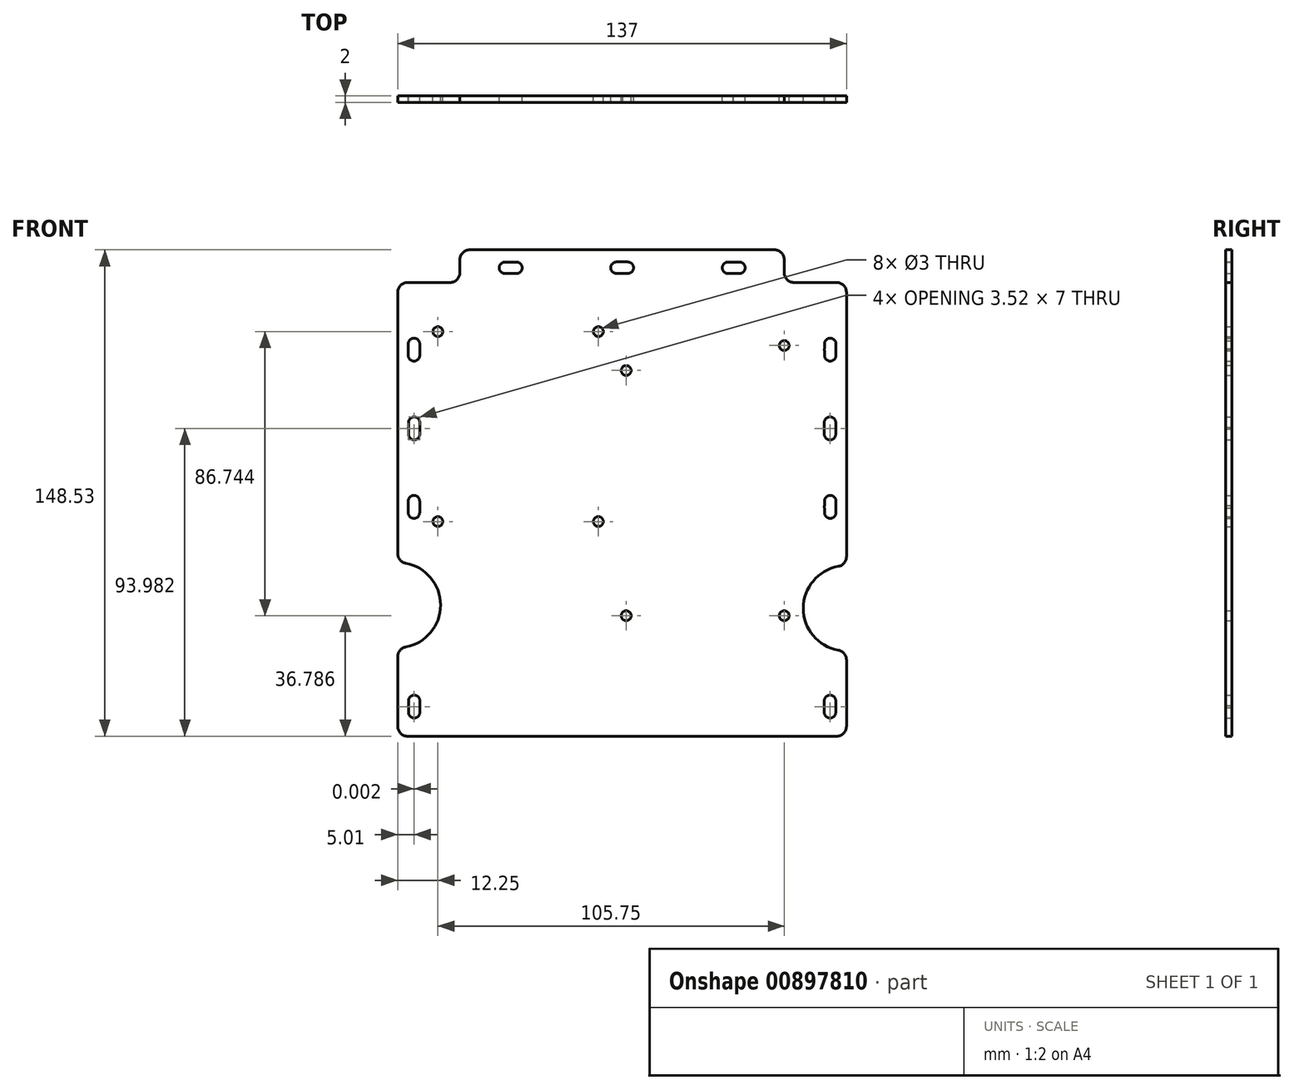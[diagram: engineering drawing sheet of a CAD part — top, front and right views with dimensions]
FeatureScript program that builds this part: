
annotation { "Feature Type Name" : "Feature", "Feature Type Description" : "" }
export const myFeature = defineFeature(function(context is Context, id is Id, definition is map)
    precondition{}
    {
        {
            var Q0;
            Q0=qCreatedBy(makeId("Front.planeOp"),FACE);
            var sketch = newSketch(context, id + "F0", { "sketchPlane" : qUnion([Q0])});
            skLineSegment(sketch, "E0", {"start": v(-49.5, 105.5) * mm, "end": v(-49.5, 101.5) * mm});
            skLineSegment(sketch, "E1", {"start": v(-52.5, 98.5) * mm, "end": v(-65.5, 98.5) * mm});
            skLineSegment(sketch, "E2", {"start": v(-68.5, 95.5) * mm, "end": v(-68.5, 15.73) * mm});
            skLineSegment(sketch, "E3", {"start": v(-46.5, 108.5) * mm, "end": v(0, 108.5) * mm});
            skLineSegment(sketch, "E4.MirrorCS", {"start": v(46.5, 108.5) * mm, "end": v(0, 108.5) * mm});
            skLineSegment(sketch, "E5.MirrorCS", {"start": v(49.5, 105.5) * mm, "end": v(49.5, 101.5) * mm});
            skLineSegment(sketch, "E6.MirrorCS", {"start": v(68.5, 95.5) * mm, "end": v(68.5, 14.76) * mm});
            skPoint(sketch, "E7.visualSharp", {"position": v(-68.5, 98.5) * mm});
            skArc(sketch, "E7.filletArc", {"start": v(-65.5, 98.5) * mm, "mid": v(-67.62, 97.62) * mm, "end": v(-68.5, 95.5) * mm});
            skPoint(sketch, "E8.visualSharp", {"position": v(-49.5, 98.5) * mm});
            skArc(sketch, "E8.filletArc", {"start": v(-52.5, 98.5) * mm, "mid": v(-50.38, 99.38) * mm, "end": v(-49.5, 101.5) * mm});
            skPoint(sketch, "E9.visualSharp", {"position": v(-49.5, 108.5) * mm});
            skArc(sketch, "E9.filletArc", {"start": v(-46.5, 108.5) * mm, "mid": v(-48.62, 107.62) * mm, "end": v(-49.5, 105.5) * mm});
            skPoint(sketch, "E10.visualSharp", {"position": v(49.5, 108.5) * mm});
            skArc(sketch, "E10.filletArc", {"start": v(49.5, 105.5) * mm, "mid": v(48.62, 107.62) * mm, "end": v(46.5, 108.5) * mm});
            skPoint(sketch, "E11.visualSharp", {"position": v(49.5, 98.5) * mm});
            skArc(sketch, "E11.filletArc", {"start": v(49.5, 101.5) * mm, "mid": v(50.38, 99.38) * mm, "end": v(52.5, 98.5) * mm});
            skPoint(sketch, "E12.visualSharp", {"position": v(68.5, 98.5) * mm});
            skArc(sketch, "E12.filletArc", {"start": v(68.5, 95.5) * mm, "mid": v(67.62, 97.62) * mm, "end": v(65.5, 98.5) * mm});
            skCircle(sketch, "E13", {"center": v(0, 103) * mm, "radius": 1.75 * mm});
            skCircle(sketch, "E14", {"center": v(-34, 103) * mm, "radius": 1.75 * mm});
            skCircle(sketch, "E15", {"center": v(34, 103) * mm, "radius": 1.75 * mm});
            skPoint(sketch, "E16.centerSnap0", {"position": v(-59, 98.5) * mm});
            skCircle(sketch, "E17", {"center": v(-63.5, 54) * mm, "radius": 1.75 * mm});
            skCircle(sketch, "E18", {"center": v(-63.5, 30) * mm, "radius": 1.75 * mm});
            skCircle(sketch, "E19", {"center": v(-63.5, 78) * mm, "radius": 1.75 * mm});
            skCircle(sketch, "E20.MirrorC", {"center": v(63.5, 78) * mm, "radius": 1.75 * mm});
            skCircle(sketch, "E21.MirrorC", {"center": v(63.5, 54) * mm, "radius": 1.75 * mm});
            skCircle(sketch, "E22.MirrorC", {"center": v(63.5, 30) * mm, "radius": 1.75 * mm});
            skCircle(sketch, "E23", {"center": v(-63.5, -31) * mm, "radius": 1.75 * mm});
            skCircle(sketch, "E24.MirrorC", {"center": v(63.5, -31) * mm, "radius": 1.75 * mm});
            skLineSegment(sketch, "E25", {"start": v(-35.75, 103) * mm, "end": v(-32.25, 103) * mm});
            skArc(sketch, "E26.0.startCap", {"start": v(-35.75, 101.25) * mm, "mid": v(-37.5, 103) * mm, "end": v(-35.75, 104.75) * mm});
            skArc(sketch, "E26.0.endCap", {"start": v(-32.25, 104.75) * mm, "mid": v(-30.5, 103) * mm, "end": v(-32.25, 101.25) * mm});
            skLineSegment(sketch, "E26.0.left", {"start": v(-35.75, 104.75) * mm, "end": v(-32.25, 104.75) * mm});
            skLineSegment(sketch, "E26.0.right", {"start": v(-35.75, 101.25) * mm, "end": v(-32.25, 101.25) * mm});
            skArc(sketch, "E27.0.startCap", {"start": v(-1.74, 101.27) * mm, "mid": v(-3.5, 103.02) * mm, "end": v(-1.74, 104.77) * mm});
            skArc(sketch, "E27.0.endCap", {"start": v(1.76, 104.77) * mm, "mid": v(3.5, 103.02) * mm, "end": v(1.76, 101.27) * mm});
            skLineSegment(sketch, "E27.0.left", {"start": v(-1.74, 104.77) * mm, "end": v(1.76, 104.77) * mm});
            skLineSegment(sketch, "E27.0.right", {"start": v(-1.74, 101.27) * mm, "end": v(1.76, 101.27) * mm});
            skArc(sketch, "E28.0.startCap", {"start": v(32.33, 101.25) * mm, "mid": v(30.58, 103) * mm, "end": v(32.33, 104.75) * mm});
            skArc(sketch, "E28.0.endCap", {"start": v(35.83, 104.75) * mm, "mid": v(37.58, 103) * mm, "end": v(35.83, 101.25) * mm});
            skLineSegment(sketch, "E28.0.left", {"start": v(32.33, 104.75) * mm, "end": v(35.83, 104.75) * mm});
            skLineSegment(sketch, "E28.0.right", {"start": v(32.33, 101.25) * mm, "end": v(35.83, 101.25) * mm});
            skLineSegment(sketch, "E29", {"start": v(-63.53, 79.75) * mm, "end": v(-63.53, 76.25) * mm});
            skArc(sketch, "E30.0.startCap", {"start": v(-65.28, 79.75) * mm, "mid": v(-63.53, 81.5) * mm, "end": v(-61.78, 79.75) * mm});
            skArc(sketch, "E30.0.endCap", {"start": v(-61.78, 76.25) * mm, "mid": v(-63.53, 74.5) * mm, "end": v(-65.28, 76.25) * mm});
            skLineSegment(sketch, "E30.0.left", {"start": v(-61.78, 79.75) * mm, "end": v(-61.78, 76.25) * mm});
            skLineSegment(sketch, "E30.0.right", {"start": v(-65.28, 79.75) * mm, "end": v(-65.28, 76.25) * mm});
            skArc(sketch, "E31.0.startCap", {"start": v(-65.23, 55.7) * mm, "mid": v(-63.48, 57.45) * mm, "end": v(-61.73, 55.7) * mm});
            skArc(sketch, "E31.0.endCap", {"start": v(-61.73, 52.2) * mm, "mid": v(-63.48, 50.45) * mm, "end": v(-65.23, 52.2) * mm});
            skLineSegment(sketch, "E31.0.left", {"start": v(-61.73, 55.7) * mm, "end": v(-61.73, 52.2) * mm});
            skLineSegment(sketch, "E31.0.right", {"start": v(-65.23, 55.7) * mm, "end": v(-65.23, 52.2) * mm});
            skArc(sketch, "E32.0.startCap", {"start": v(-65.3, 31.74) * mm, "mid": v(-63.54, 33.5) * mm, "end": v(-61.8, 31.74) * mm});
            skArc(sketch, "E32.0.endCap", {"start": v(-61.8, 28.24) * mm, "mid": v(-63.54, 26.5) * mm, "end": v(-65.3, 28.24) * mm});
            skLineSegment(sketch, "E32.0.left", {"start": v(-61.8, 31.74) * mm, "end": v(-61.8, 28.24) * mm});
            skLineSegment(sketch, "E32.0.right", {"start": v(-65.3, 31.74) * mm, "end": v(-65.3, 28.24) * mm});
            skArc(sketch, "E33.MirrorCS", {"start": v(65.28, 79.75) * mm, "mid": v(63.53, 81.5) * mm, "end": v(61.78, 79.75) * mm});
            skLineSegment(sketch, "E34.MirrorCS", {"start": v(61.78, 79.75) * mm, "end": v(61.78, 76.25) * mm});
            skArc(sketch, "E35.MirrorCS", {"start": v(61.78, 76.25) * mm, "mid": v(63.53, 74.5) * mm, "end": v(65.28, 76.25) * mm});
            skLineSegment(sketch, "E36.MirrorCS", {"start": v(65.28, 79.75) * mm, "end": v(65.28, 76.25) * mm});
            skArc(sketch, "E37.MirrorCS", {"start": v(65.23, 55.7) * mm, "mid": v(63.48, 57.45) * mm, "end": v(61.73, 55.7) * mm});
            skLineSegment(sketch, "E38.MirrorCS", {"start": v(61.73, 55.7) * mm, "end": v(61.73, 52.2) * mm});
            skLineSegment(sketch, "E39.MirrorCS", {"start": v(65.23, 55.7) * mm, "end": v(65.23, 52.2) * mm});
            skArc(sketch, "E40.MirrorCS", {"start": v(61.73, 52.2) * mm, "mid": v(63.48, 50.45) * mm, "end": v(65.23, 52.2) * mm});
            skArc(sketch, "E41.MirrorCS", {"start": v(65.3, 31.74) * mm, "mid": v(63.54, 33.5) * mm, "end": v(61.8, 31.74) * mm});
            skLineSegment(sketch, "E42.MirrorCS", {"start": v(61.8, 31.74) * mm, "end": v(61.8, 28.24) * mm});
            skArc(sketch, "E43.MirrorCS", {"start": v(61.8, 28.24) * mm, "mid": v(63.54, 26.5) * mm, "end": v(65.3, 28.24) * mm});
            skLineSegment(sketch, "E44.MirrorCS", {"start": v(65.3, 31.74) * mm, "end": v(65.3, 28.24) * mm});
            skArc(sketch, "E45.0.startCap", {"start": v(-65.23, -29.25) * mm, "mid": v(-63.48, -27.5) * mm, "end": v(-61.73, -29.25) * mm});
            skArc(sketch, "E45.0.endCap", {"start": v(-61.73, -32.75) * mm, "mid": v(-63.48, -34.5) * mm, "end": v(-65.23, -32.75) * mm});
            skLineSegment(sketch, "E45.0.left", {"start": v(-61.73, -29.25) * mm, "end": v(-61.73, -32.75) * mm});
            skLineSegment(sketch, "E45.0.right", {"start": v(-65.23, -29.25) * mm, "end": v(-65.23, -32.75) * mm});
            skArc(sketch, "E46.MirrorCS", {"start": v(65.23, -29.25) * mm, "mid": v(63.48, -27.5) * mm, "end": v(61.73, -29.25) * mm});
            skLineSegment(sketch, "E47.MirrorCS", {"start": v(61.73, -29.25) * mm, "end": v(61.73, -32.75) * mm});
            skArc(sketch, "E48.MirrorCS", {"start": v(61.73, -32.75) * mm, "mid": v(63.48, -34.5) * mm, "end": v(65.23, -32.75) * mm});
            skLineSegment(sketch, "E49.MirrorCS", {"start": v(65.23, -29.25) * mm, "end": v(65.23, -32.75) * mm});
            skCircle(sketch, "E50", {"center": v(-56.25, 83.5) * mm, "radius": 1.5 * mm});
            skCircle(sketch, "E51", {"center": v(-56.25, 25.5) * mm, "radius": 1.5 * mm});
            skCircle(sketch, "E52", {"center": v(-7.25, 25.5) * mm, "radius": 1.5 * mm});
            skCircle(sketch, "E53", {"center": v(-7.25, 83.5) * mm, "radius": 1.5 * mm});
            skPoint(sketch, "E54.startSnap0", {"position": v(-68.42, 0) * mm});
            skArc(sketch, "E55", {"start": v(-66.05, 12.78) * mm, "mid": v(-55.42, 0) * mm, "end": v(-66.05, -12.78) * mm});
            skPoint(sketch, "E56.visualSharp", {"position": v(-68.5, 13) * mm});
            skArc(sketch, "E56.filletArc", {"start": v(-68.5, 15.73) * mm, "mid": v(-67.8, 13.81) * mm, "end": v(-66.05, 12.78) * mm});
            skPoint(sketch, "E57.visualSharp", {"position": v(-68.5, -13) * mm});
            skArc(sketch, "E57.filletArc", {"start": v(-66.05, -12.78) * mm, "mid": v(-67.8, -13.81) * mm, "end": v(-68.5, -15.73) * mm});
            skArc(sketch, "E58", {"start": v(66.03, 11.81) * mm, "mid": v(55.32, -0.98) * mm, "end": v(66.03, -13.78) * mm});
            skPoint(sketch, "E59.visualSharp", {"position": v(68.5, 12.01) * mm});
            skArc(sketch, "E59.filletArc", {"start": v(66.03, 11.81) * mm, "mid": v(67.8, 12.84) * mm, "end": v(68.5, 14.76) * mm});
            skPoint(sketch, "E60.visualSharp", {"position": v(68.5, -13.98) * mm});
            skArc(sketch, "E60.filletArc", {"start": v(68.5, -16.73) * mm, "mid": v(67.8, -14.8) * mm, "end": v(66.03, -13.78) * mm});
            skCircle(sketch, "E61", {"center": v(1.25, 71.66) * mm, "radius": 1.5 * mm});
            skCircle(sketch, "E62", {"center": v(1.25, -3.24) * mm, "radius": 1.5 * mm});
            skCircle(sketch, "E63", {"center": v(49.5, 79.26) * mm, "radius": 1.5 * mm});
            skCircle(sketch, "E64", {"center": v(49.5, -3.24) * mm, "radius": 1.5 * mm});
            skLineSegment(sketch, "E65", {"start": v(52.5, 98.5) * mm, "end": v(65.5, 98.5) * mm});
            skLineSegment(sketch, "E66", {"start": v(-65.5, -40.03) * mm, "end": v(65.5, -40.03) * mm});
            skLineSegment(sketch, "E67", {"start": v(-68.5, -15.73) * mm, "end": v(-68.5, -37.03) * mm});
            skLineSegment(sketch, "E68", {"start": v(68.5, -16.73) * mm, "end": v(68.5, -37.03) * mm});
            skPoint(sketch, "E69.visualSharp", {"position": v(-68.5, -40.03) * mm});
            skArc(sketch, "E69.filletArc", {"start": v(-68.5, -37.03) * mm, "mid": v(-67.62, -39.15) * mm, "end": v(-65.5, -40.03) * mm});
            skPoint(sketch, "E70.visualSharp", {"position": v(68.5, -40.03) * mm});
            skArc(sketch, "E70.filletArc", {"start": v(65.5, -40.03) * mm, "mid": v(67.62, -39.15) * mm, "end": v(68.5, -37.03) * mm});
            skSolve(sketch);
        }
        {
            var Q0;
            Q0=makeQuery(id+"F0.imprint","IMPRINT",FACE,{"disambiguationData":[TD([[makeQuery(id+"F0.imprint","IMPRINT",EDGE,{"derivedFrom":sQuery(id+"F0.wireOp",EDGE,"E0")}),1.0]])]});
            extrude(context, id + "F1", {"entities" : qUnion([Q0]), "depth" : 2 * mm, "offsetDistance" : 25 * mm});
        }
    });
